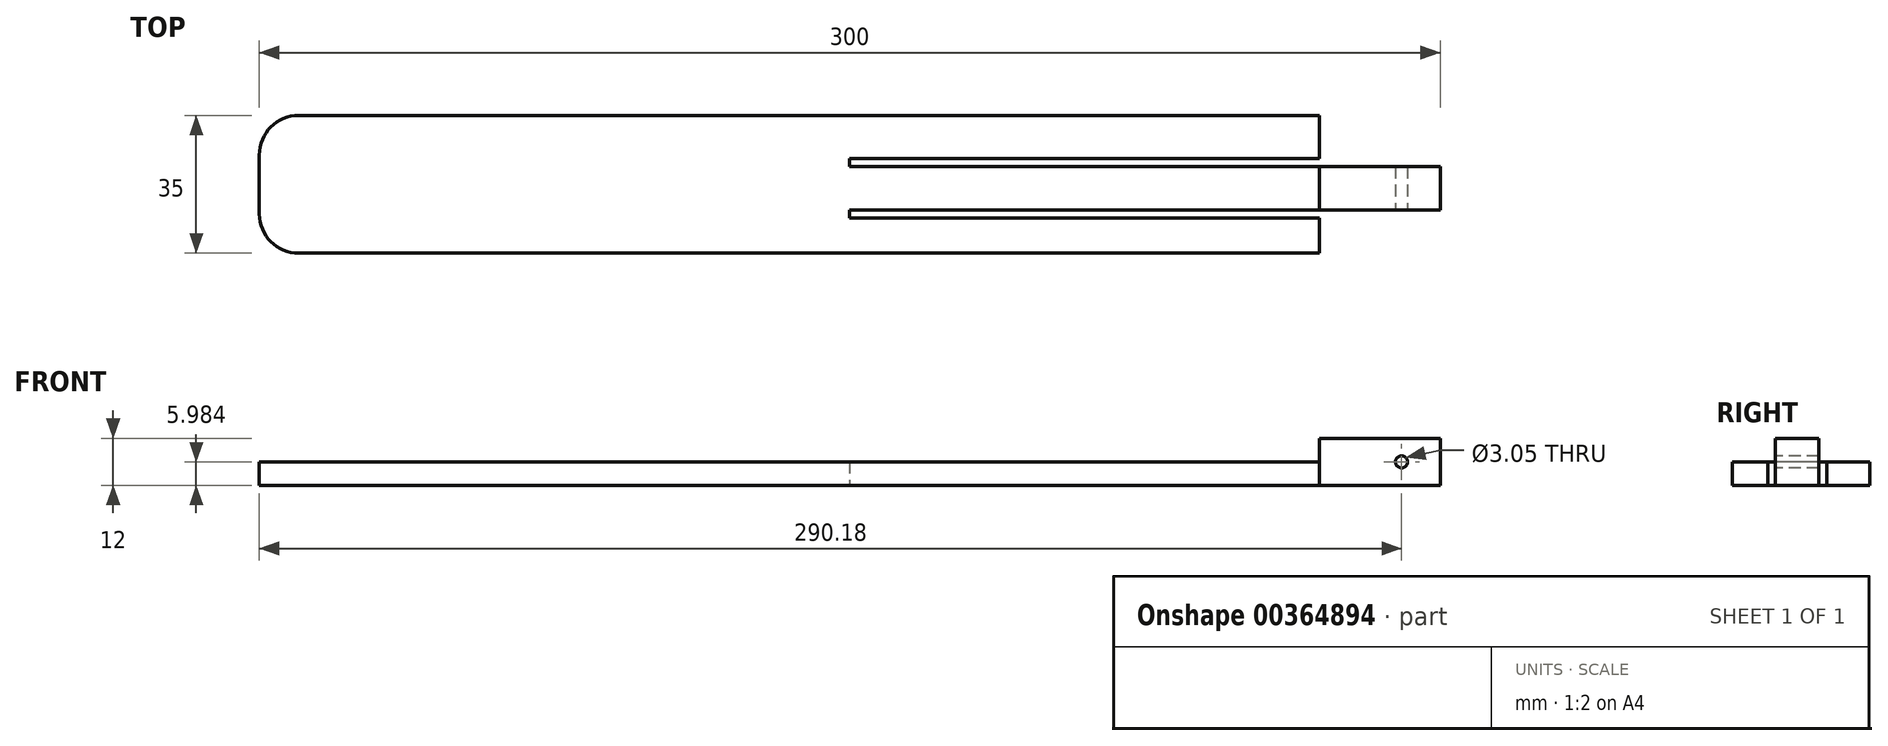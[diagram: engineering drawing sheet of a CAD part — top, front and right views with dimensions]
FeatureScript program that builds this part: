
annotation { "Feature Type Name" : "Feature", "Feature Type Description" : "" }
export const myFeature = defineFeature(function(context is Context, id is Id, definition is map)
    precondition{}
    {
        {
            var Q0;
            Q0=qCreatedBy(makeId("Top.planeOp"),FACE);
            var sketch = newSketch(context, id + "F0", { "sketchPlane" : qUnion([Q0])});
            skLineSegment(sketch, "E0.bottom", {"start": v(-150, 17.5) * mm, "end": v(119.34, 17.5) * mm});
            skLineSegment(sketch, "E0.top", {"start": v(-150, -17.5) * mm, "end": v(119.34, -17.5) * mm});
            skLineSegment(sketch, "E0.left", {"start": v(-150, 17.5) * mm, "end": v(-150, -17.5) * mm});
            skPoint(sketch, "E0.middle", {"position": v(0, 0) * mm});
            skLineSegment(sketch, "E1", {"start": v(0, 6.5) * mm, "end": v(119.34, 6.5) * mm});
            skLineSegment(sketch, "E2", {"start": v(0, 4.5) * mm, "end": v(150, 4.5) * mm});
            skLineSegment(sketch, "E3", {"start": v(0, -8.5) * mm, "end": v(119.34, -8.5) * mm});
            skLineSegment(sketch, "E4", {"start": v(0, -6.5) * mm, "end": v(150, -6.5) * mm});
            skLineSegment(sketch, "E5", {"start": v(0, -6.5) * mm, "end": v(0, -8.5) * mm});
            skLineSegment(sketch, "E6", {"start": v(0, 6.5) * mm, "end": v(0, 4.5) * mm});
            skLineSegment(sketch, "E7.trimOffspring", {"start": v(150, 4.5) * mm, "end": v(150, -6.5) * mm});
            skLineSegment(sketch, "E8", {"start": v(119.34, 17.5) * mm, "end": v(119.34, 6.5) * mm});
            skPoint(sketch, "E0.right.start.orphan", {"position": v(150, 17.5) * mm});
            skPoint(sketch, "E9.trimOffspring.start.orphan", {"position": v(150, -8.5) * mm});
            skPoint(sketch, "E10.orphan", {"position": v(150, -17.5) * mm});
            skLineSegment(sketch, "E11.trimOffspring", {"start": v(119.34, -8.5) * mm, "end": v(119.34, -17.5) * mm});
            skSolve(sketch);
        }
        {
            var Q0;
            Q0=makeQuery(id+"F0.imprint","IMPRINT",FACE,{"disambiguationData":[TD([[makeQuery(id+"F0.imprint","IMPRINT",EDGE,{"derivedFrom":sQuery(id+"F0.wireOp",EDGE,"E0.bottom")}),-1.0]])]});
            extrude(context, id + "F1", {"entities" : qUnion([Q0]), "depth" : 6 * mm});
        }
        {
            var Q0;
            Q0=makeQuery(id+"F1.opExtrude","SWEPT_EDGE",EDGE,{"disambiguationData":[OSD([sQuery(id+"F0.wireOp",EDGE,"E0.top"),sQuery(id+"F0.wireOp",EDGE,"E0.left")])]});
            var Q1;
            Q1=makeQuery(id+"F1.opExtrude","SWEPT_EDGE",EDGE,{"disambiguationData":[OSD([sQuery(id+"F0.wireOp",EDGE,"E0.bottom"),sQuery(id+"F0.wireOp",EDGE,"E0.left")])]});
            fillet(context, id + "F2", {"entities" : qUnion([Q0, Q1]), "radius" : 10 * mm, "tangentPropagation" : true, "allowEdgeOverflow" : false});
        }
        {
            var Q0;
            Q0=makeQuery(id+"F1.opExtrude","CAP_FACE",FACE,{"disambiguationData":[OSD([sQuery(id+"F0.wireOp",EDGE,"E0.bottom"),sQuery(id+"F0.wireOp",EDGE,"E0.top"),sQuery(id+"F0.wireOp",EDGE,"E0.left"),sQuery(id+"F0.wireOp",EDGE,"E1"),sQuery(id+"F0.wireOp",EDGE,"E2"),sQuery(id+"F0.wireOp",EDGE,"E3"),sQuery(id+"F0.wireOp",EDGE,"E4"),sQuery(id+"F0.wireOp",EDGE,"E5"),sQuery(id+"F0.wireOp",EDGE,"E6"),sQuery(id+"F0.wireOp",EDGE,"E7.trimOffspring"),sQuery(id+"F0.wireOp",EDGE,"E8"),sQuery(id+"F0.wireOp",EDGE,"E11.trimOffspring")])],"isStart":false});
            var sketch = newSketch(context, id + "F3", { "sketchPlane" : qUnion([Q0])});
            skLineSegment(sketch, "E12.bottom", {"start": v(119.34, 4.5) * mm, "end": v(150, 4.5) * mm});
            skLineSegment(sketch, "E12.top", {"start": v(119.34, -6.5) * mm, "end": v(150, -6.5) * mm});
            skLineSegment(sketch, "E12.left", {"start": v(119.34, 4.5) * mm, "end": v(119.34, -6.5) * mm});
            skLineSegment(sketch, "E12.right", {"start": v(150, 4.5) * mm, "end": v(150, -6.5) * mm});
            skSolve(sketch);
        }
        {
            var Q0;
            Q0=makeQuery(id+"F3.imprint","IMPRINT",FACE,{"disambiguationData":[TD([[makeQuery(id+"F3.imprint","IMPRINT",EDGE,{"derivedFrom":sQuery(id+"F3.wireOp",EDGE,"E12.bottom")}),-1.0]])]});
            extrude(context, id + "F4", {"entities" : qUnion([Q0]), "operationType" : NewBodyOperationType.ADD, "depth" : 6 * mm});
        }
        {
            var Q0;
            Q0=makeQuery(id+"F4.boolean.opBoolean","MERGE",FACE,{"derivedFrom":[makeQuery(id+"F1.opExtrude","SWEPT_FACE",FACE,{"disambiguationData":[OSD([sQuery(id+"F0.wireOp",EDGE,"E4")])]}),makeQuery(id+"F4.opExtrude","SWEPT_FACE",FACE,{"disambiguationData":[OSD([sQuery(id+"F3.wireOp",EDGE,"E12.top")])]})]});
            var sketch = newSketch(context, id + "F5", { "sketchPlane" : qUnion([Q0])});
            skCircle(sketch, "E13", {"center": v(140.18, 5.98) * mm, "radius": 1.53 * mm});
            skSolve(sketch);
        }
        {
            var Q0;
            Q0=makeQuery(id+"F5.imprint","IMPRINT",FACE,{"disambiguationData":[TD([[makeQuery(id+"F5.imprint","IMPRINT",EDGE,{"derivedFrom":sQuery(id+"F5.wireOp",EDGE,"E13")}),1.0]])]});
            extrude(context, id + "F6", {"entities" : qUnion([Q0]), "operationType" : NewBodyOperationType.REMOVE, "oppositeDirection" : true, "depth" : 11.4 * mm});
        }
    });
